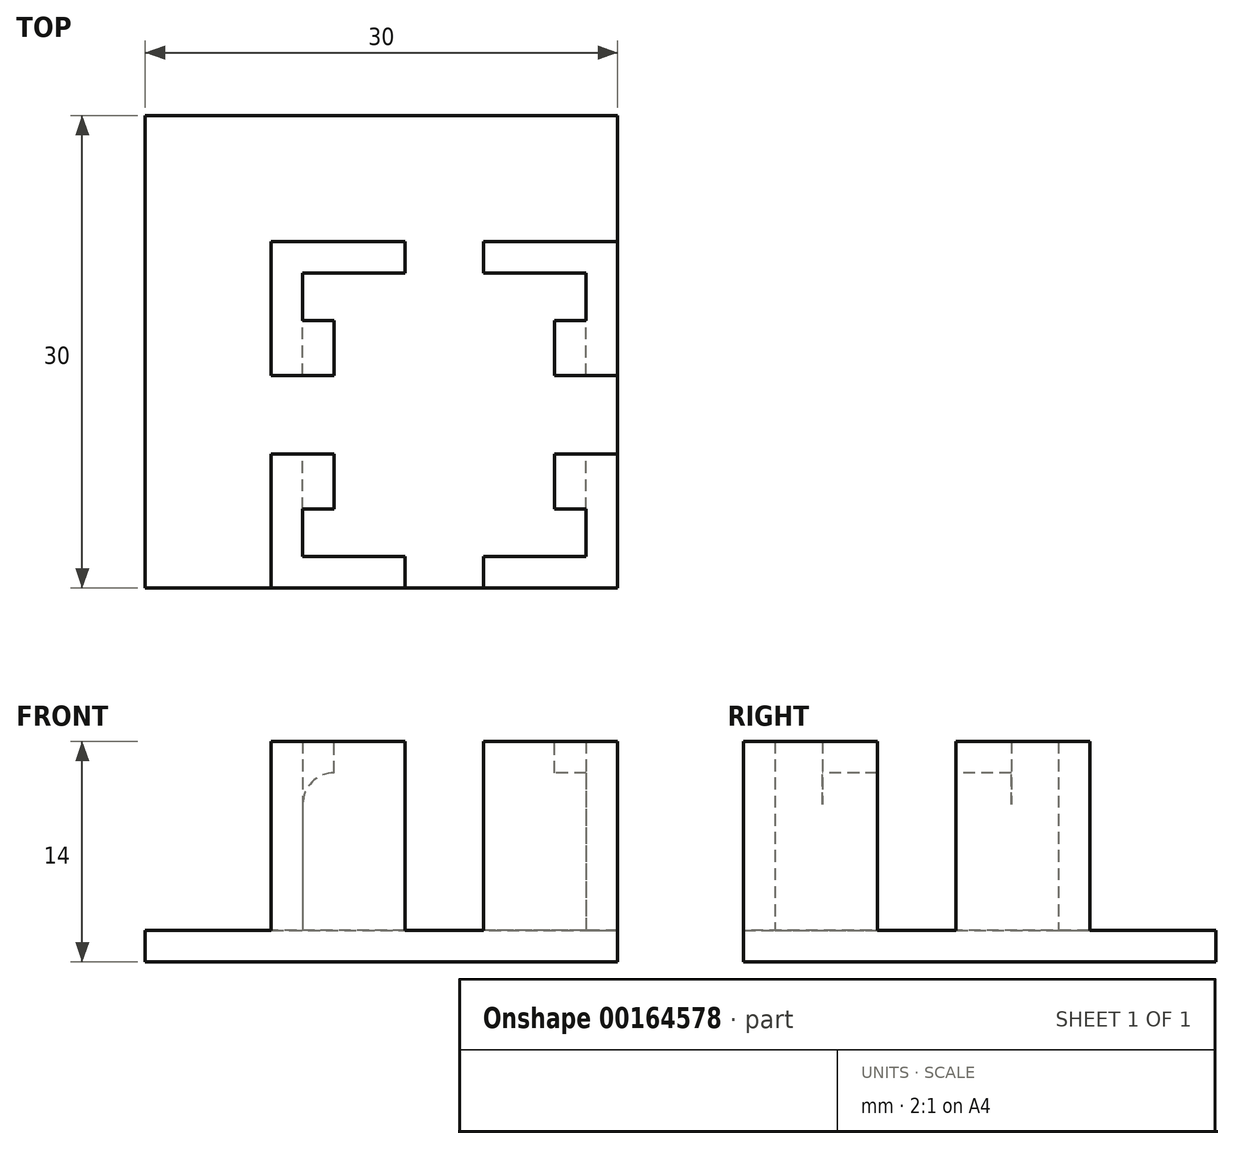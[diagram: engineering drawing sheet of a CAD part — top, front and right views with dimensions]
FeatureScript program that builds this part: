
annotation { "Feature Type Name" : "Feature", "Feature Type Description" : "" }
export const myFeature = defineFeature(function(context is Context, id is Id, definition is map)
    precondition{}
    {
        {
            var Q0;
            Q0=qCreatedBy(makeId("Top.planeOp"),FACE);
            var sketch = newSketch(context, id + "F0", { "sketchPlane" : qUnion([Q0])});
            skLineSegment(sketch, "E0.bottom", {"start": v(0, 0) * mm, "end": v(30, 0) * mm});
            skLineSegment(sketch, "E0.top", {"start": v(0, -30) * mm, "end": v(30, -30) * mm});
            skLineSegment(sketch, "E0.left", {"start": v(0, 0) * mm, "end": v(0, -30) * mm});
            skLineSegment(sketch, "E0.right", {"start": v(30, 0) * mm, "end": v(30, -30) * mm});
            skSolve(sketch);
        }
        {
            var Q0;
            Q0=qSketchRegion(id+"F0",true);
            extrude(context, id + "F1", {"entities" : qUnion([Q0]), "depth" : 2 * mm});
        }
        {
            var Q0;
            Q0=makeQuery(id+"F1.opExtrude","CAP_FACE",FACE,{"disambiguationData":[OSD([sQuery(id+"F0.wireOp",EDGE,"E0.bottom"),sQuery(id+"F0.wireOp",EDGE,"E0.top"),sQuery(id+"F0.wireOp",EDGE,"E0.left"),sQuery(id+"F0.wireOp",EDGE,"E0.right")])],"isStart":false});
            var sketch = newSketch(context, id + "F2", { "sketchPlane" : qUnion([Q0])});
            skLineSegment(sketch, "E1.bottom", {"start": v(30, -30) * mm, "end": v(8, -30) * mm});
            skLineSegment(sketch, "E1.top", {"start": v(30, -8) * mm, "end": v(8, -8) * mm});
            skLineSegment(sketch, "E1.left", {"start": v(30, -30) * mm, "end": v(30, -8) * mm});
            skLineSegment(sketch, "E1.right", {"start": v(8, -30) * mm, "end": v(8, -8) * mm});
            skLineSegment(sketch, "E2.0", {"start": v(28, -10) * mm, "end": v(10, -10) * mm});
            skLineSegment(sketch, "E2.1", {"start": v(28, -28) * mm, "end": v(28, -10) * mm});
            skLineSegment(sketch, "E2.2", {"start": v(28, -28) * mm, "end": v(10, -28) * mm});
            skLineSegment(sketch, "E2.3", {"start": v(10, -28) * mm, "end": v(10, -10) * mm});
            skSolve(sketch);
        }
        {
            var Q0;
            Q0=qSketchRegion(id+"F2",true);
            extrude(context, id + "F3", {"entities" : qUnion([Q0]), "operationType" : NewBodyOperationType.ADD, "depth" : 10 * mm});
        }
        {
            var Q0;
            Q0=makeQuery(id+"F3.opExtrude","CAP_FACE",FACE,{"disambiguationData":[OSD([sQuery(id+"F2.wireOp",EDGE,"E1.bottom"),sQuery(id+"F2.wireOp",EDGE,"E1.top"),sQuery(id+"F2.wireOp",EDGE,"E1.left"),sQuery(id+"F2.wireOp",EDGE,"E1.right"),sQuery(id+"F2.wireOp",EDGE,"E2.0"),sQuery(id+"F2.wireOp",EDGE,"E2.1"),sQuery(id+"F2.wireOp",EDGE,"E2.2"),sQuery(id+"F2.wireOp",EDGE,"E2.3")])],"isStart":false});
            var sketch = newSketch(context, id + "F4", { "sketchPlane" : qUnion([Q0])});
            skLineSegment(sketch, "E3.0", {"start": v(30, -8) * mm, "end": v(8, -8) * mm});
            skLineSegment(sketch, "E3.1", {"start": v(8, -30) * mm, "end": v(8, -8) * mm});
            skLineSegment(sketch, "E3.2", {"start": v(10, -28) * mm, "end": v(10, -10) * mm});
            skLineSegment(sketch, "E3.3", {"start": v(8, -30) * mm, "end": v(30, -30) * mm});
            skLineSegment(sketch, "E3.4", {"start": v(28, -28) * mm, "end": v(10, -28) * mm});
            skLineSegment(sketch, "E3.5", {"start": v(28, -28) * mm, "end": v(28, -10) * mm});
            skLineSegment(sketch, "E3.6", {"start": v(30, -8) * mm, "end": v(30, -30) * mm});
            skLineSegment(sketch, "E3.7", {"start": v(28, -10) * mm, "end": v(10, -10) * mm});
            skLineSegment(sketch, "E4.bottom", {"start": v(12, -10) * mm, "end": v(26, -10) * mm});
            skLineSegment(sketch, "E4.top", {"start": v(12, -12) * mm, "end": v(26, -12) * mm});
            skLineSegment(sketch, "E4.left", {"start": v(12, -10) * mm, "end": v(12, -12) * mm});
            skLineSegment(sketch, "E4.right", {"start": v(26, -10) * mm, "end": v(26, -12) * mm});
            skLineSegment(sketch, "E5.bottom", {"start": v(13, -28) * mm, "end": v(26, -28) * mm});
            skLineSegment(sketch, "E5.top", {"start": v(13, -26) * mm, "end": v(26, -26) * mm});
            skLineSegment(sketch, "E5.left", {"start": v(13, -28) * mm, "end": v(13, -26) * mm});
            skLineSegment(sketch, "E5.right", {"start": v(26, -28) * mm, "end": v(26, -26) * mm});
            skLineSegment(sketch, "E6.bottom", {"start": v(10, -13) * mm, "end": v(12, -13) * mm});
            skLineSegment(sketch, "E6.top", {"start": v(10, -25) * mm, "end": v(12, -25) * mm});
            skLineSegment(sketch, "E6.left", {"start": v(10, -13) * mm, "end": v(10, -25) * mm});
            skLineSegment(sketch, "E6.right", {"start": v(12, -13) * mm, "end": v(12, -25) * mm});
            skLineSegment(sketch, "E7.bottom", {"start": v(28, -13) * mm, "end": v(26, -13) * mm});
            skLineSegment(sketch, "E7.top", {"start": v(28, -25) * mm, "end": v(26, -25) * mm});
            skLineSegment(sketch, "E7.left", {"start": v(28, -13) * mm, "end": v(28, -25) * mm});
            skLineSegment(sketch, "E7.right", {"start": v(26, -13) * mm, "end": v(26, -25) * mm});
            skSolve(sketch);
        }
        {
            var Q0;
            Q0=qSketchRegion(id+"F4",true);
            var Q1;
            Q1=makeQuery(id+"F4.imprint","IMPRINT",FACE,{"disambiguationData":[TD([[makeQuery(id+"F4.imprint","IMPRINT",EDGE,{"derivedFrom":sQuery(id+"F4.wireOp",EDGE,"E6.bottom")}),-1.0]])]});
            var Q2;
            Q2=makeQuery(id+"F4.imprint","IMPRINT",FACE,{"disambiguationData":[TD([[makeQuery(id+"F4.imprint","IMPRINT",EDGE,{"derivedFrom":sQuery(id+"F4.wireOp",EDGE,"E4.bottom")}),1.0]])]});
            var Q3;
            Q3=makeQuery(id+"F4.imprint","IMPRINT",FACE,{"disambiguationData":[TD([[makeQuery(id+"F4.imprint","IMPRINT",EDGE,{"derivedFrom":sQuery(id+"F4.wireOp",EDGE,"E7.bottom")}),1.0]])]});
            var Q4;
            Q4=makeQuery(id+"F4.imprint","IMPRINT",FACE,{"disambiguationData":[TD([[makeQuery(id+"F4.imprint","IMPRINT",EDGE,{"derivedFrom":sQuery(id+"F4.wireOp",EDGE,"E5.bottom")}),-1.0]])]});
            extrude(context, id + "F5", {"entities" : qUnion([Q0, Q1, Q2, Q3, Q4]), "operationType" : NewBodyOperationType.ADD, "depth" : 2 * mm});
        }
        {
            var Q0;
            Q0=makeQuery(id+"F3.opExtrude","CAP_EDGE",EDGE,{"disambiguationData":[OSD([sQuery(id+"F2.wireOp",EDGE,"E2.3")])],"isStart":false});
            var Q1;
            Q1=makeQuery(id+"F3.opExtrude","CAP_EDGE",EDGE,{"disambiguationData":[OSD([sQuery(id+"F2.wireOp",EDGE,"E2.1")])],"isStart":false});
            var Q2;
            Q2=makeQuery(id+"F3.opExtrude","CAP_EDGE",EDGE,{"disambiguationData":[OSD([sQuery(id+"F2.wireOp",EDGE,"E2.0")])],"isStart":false});
            var Q3;
            Q3=makeQuery(id+"F3.opExtrude","CAP_EDGE",EDGE,{"disambiguationData":[OSD([sQuery(id+"F2.wireOp",EDGE,"E2.2")])],"isStart":false});
            fillet(context, id + "F6", {"entities" : qUnion([Q0, Q1, Q2, Q3]), "radius" : 2 * mm, "tangentPropagation" : true, "allowEdgeOverflow" : false});
        }
        {
            var Q0;
            Q0=makeQuery(id+"F5.opExtrude","CAP_FACE",FACE,{"disambiguationData":[OSD([sQuery(id+"F4.wireOp",EDGE,"E3.0"),sQuery(id+"F4.wireOp",EDGE,"E3.1"),sQuery(id+"F4.wireOp",EDGE,"E3.2"),sQuery(id+"F4.wireOp",EDGE,"E3.3"),sQuery(id+"F4.wireOp",EDGE,"E3.4"),sQuery(id+"F4.wireOp",EDGE,"E3.5"),sQuery(id+"F4.wireOp",EDGE,"E3.6"),sQuery(id+"F4.wireOp",EDGE,"E3.7"),sQuery(id+"F4.wireOp",EDGE,"E4.top"),sQuery(id+"F4.wireOp",EDGE,"E4.left"),sQuery(id+"F4.wireOp",EDGE,"E4.right"),sQuery(id+"F4.wireOp",EDGE,"E5.top"),sQuery(id+"F4.wireOp",EDGE,"E5.left"),sQuery(id+"F4.wireOp",EDGE,"E5.right"),sQuery(id+"F4.wireOp",EDGE,"E6.bottom"),sQuery(id+"F4.wireOp",EDGE,"E6.top"),sQuery(id+"F4.wireOp",EDGE,"E6.right"),sQuery(id+"F4.wireOp",EDGE,"E7.bottom"),sQuery(id+"F4.wireOp",EDGE,"E7.top"),sQuery(id+"F4.wireOp",EDGE,"E7.right")])],"isStart":false});
            var sketch = newSketch(context, id + "F7", { "sketchPlane" : qUnion([Q0])});
            skPoint(sketch, "E8.0", {"position": v(19, -8) * mm});
            skPoint(sketch, "E8.1", {"position": v(8, -19) * mm});
            skLineSegment(sketch, "E9", {"start": v(19, -8) * mm, "end": v(19, -32.55) * mm, "construction": true});
            skLineSegment(sketch, "E10", {"start": v(8, -19) * mm, "end": v(33.23, -19) * mm, "construction": true});
            skPoint(sketch, "E10.endSnap0", {"position": v(30, -19) * mm});
            skLineSegment(sketch, "E11.bottom", {"start": v(34, -21.5) * mm, "end": v(4, -21.5) * mm});
            skLineSegment(sketch, "E11.top", {"start": v(34, -16.5) * mm, "end": v(4, -16.5) * mm});
            skLineSegment(sketch, "E11.left", {"start": v(34, -21.5) * mm, "end": v(34, -16.5) * mm});
            skLineSegment(sketch, "E11.right", {"start": v(4, -21.5) * mm, "end": v(4, -16.5) * mm});
            skPoint(sketch, "E11.middle", {"position": v(19, -19) * mm});
            skLineSegment(sketch, "E12.bottom", {"start": v(21.5, -4) * mm, "end": v(16.5, -4) * mm});
            skLineSegment(sketch, "E12.top", {"start": v(21.5, -34) * mm, "end": v(16.5, -34) * mm});
            skLineSegment(sketch, "E12.left", {"start": v(21.5, -4) * mm, "end": v(21.5, -34) * mm});
            skLineSegment(sketch, "E12.right", {"start": v(16.5, -4) * mm, "end": v(16.5, -34) * mm});
            skSolve(sketch);
        }
        {
            var Q0;
            Q0=qSketchRegion(id+"F7",true);
            var Q1;
            {var subQ0=sQuery(id+"F0.wireOp",EDGE,"E0.right");var subQ1=sQuery(id+"F0.wireOp",EDGE,"E0.left");var subQ2=sQuery(id+"F0.wireOp",EDGE,"E0.top");var subQ3=sQuery(id+"F0.wireOp",EDGE,"E0.bottom");Q1=makeQuery(id+"F3.boolean.opBoolean","SPLIT",FACE,{"disambiguationData":[TD([makeQuery(id+"F1.opExtrude","SWEPT_FACE",FACE,{"disambiguationData":[OSD([subQ3])]})])],"derivedFrom":makeQuery(id+"F1.opExtrude","CAP_FACE",FACE,{"disambiguationData":[OSD([subQ3,subQ2,subQ1,subQ0])],"isStart":false})});}
            extrude(context, id + "F8", {"entities" : qUnion([Q0]), "operationType" : NewBodyOperationType.REMOVE, "endBound" : BoundingType.UP_TO_SURFACE, "oppositeDirection" : true, "endBoundEntityFace" : qUnion([Q1]), "depth" : 25 * mm});
        }
    });
